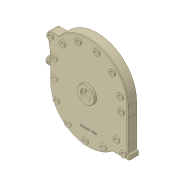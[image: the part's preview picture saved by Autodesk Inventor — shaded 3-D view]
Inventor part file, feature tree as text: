
AUTODESK INVENTOR PART (.ipt)
format: ipt  version: 2016 (Build 200138000, 138)  size: 924,672 bytes
history: native  units: in
note: dims shown in document units (in); Inventor stores cm internally (conversion verified against a paired STEP export)
features: thread x6
ambient origin geometry x8: Origin, YZ Plane, XZ Plane, XY Plane, X Axis, Y Axis, Z Axis, Center Point
bodies: Solid2 (feature_tree), Solid1 (feature_tree)
feature tree (6):
  thread  "Thread1"  [1 undecoded]
  thread  "Thread2"  [1 undecoded]
  thread  "Thread3"  [1 undecoded]
  thread  "Thread4"  [1 undecoded]
  thread  "Thread5"  [1 undecoded]
  thread  "Thread6"  [1 undecoded]
note: 6 required parameter values undecoded (feature->parameter linkage not recoverable at this tier; creation-order binding heuristic only, values carry confidence <= 0.55)
